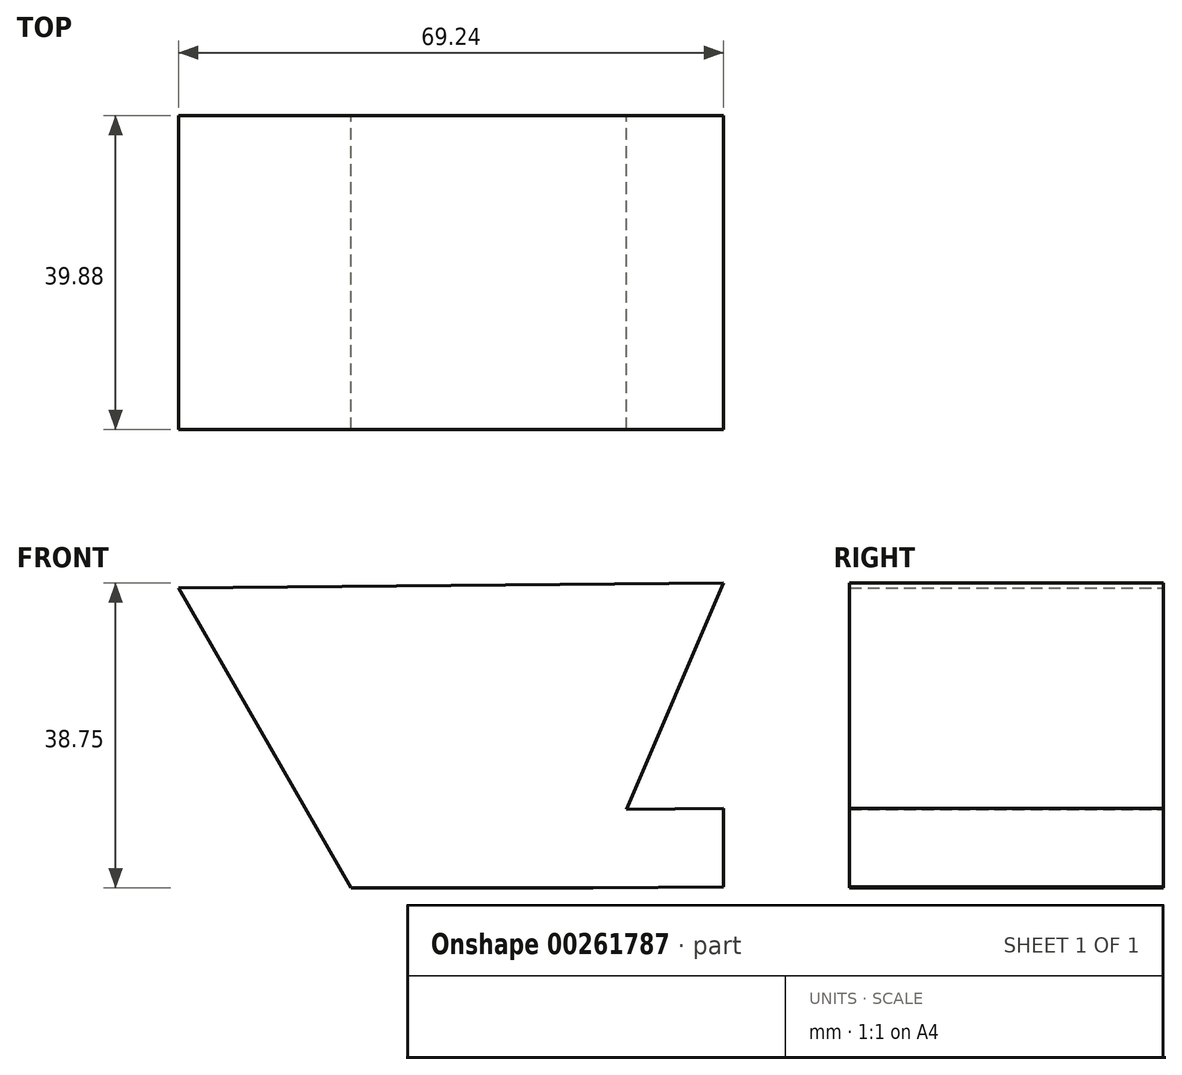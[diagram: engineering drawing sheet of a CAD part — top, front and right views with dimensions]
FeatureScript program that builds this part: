
annotation { "Feature Type Name" : "Feature", "Feature Type Description" : "" }
export const myFeature = defineFeature(function(context is Context, id is Id, definition is map)
    precondition{}
    {
        {
            var Q0;
            Q0=qCreatedBy(makeId("Front.planeOp"),FACE);
            var sketch = newSketch(context, id + "F0", { "sketchPlane" : qUnion([Q0])});
            skLineSegment(sketch, "E0", {"start": v(-55.18, 7.8) * mm, "end": v(-33.26, -30.31) * mm});
            skLineSegment(sketch, "E1", {"start": v(-33.26, -30.31) * mm, "end": v(-2.56, -30.31) * mm});
            skLineSegment(sketch, "E2", {"start": v(-2.56, -30.31) * mm, "end": v(14.06, 8.44) * mm});
            skLineSegment(sketch, "E3", {"start": v(-55.18, 7.8) * mm, "end": v(14.06, 8.44) * mm});
            skLineSegment(sketch, "E4", {"start": v(-2.56, -30.31) * mm, "end": v(14.06, -30.16) * mm});
            skLineSegment(sketch, "E5", {"start": v(14.06, -20.2) * mm, "end": v(0, -20.34) * mm});
            skLineSegment(sketch, "E6", {"start": v(0, -20.34) * mm, "end": v(14.06, -20.2) * mm});
            skLineSegment(sketch, "E7", {"start": v(14.06, -30.16) * mm, "end": v(14.06, -20.2) * mm});
            skSolve(sketch);
        }
        {
            var Q0;
            Q0 = qSketchRegion(id + "F0", true);
            extrude(context, id + "F1", {"entities" : qUnion([Q0]), "depth" : 39.88 * mm});
        }
    });
